# Revit family: BE_85013_de_DE
name_source: partatom
category: Leuchten
units: mm (PartAtom-declared; Revit-internal decimal feet)

## family parameters
Basisbauteil = Fläche
Beim Laden mit Abzugskörper schneiden = Ja
Bemaßung runder Anschluss = Durchmesser verwenden
Gemeinsam genutzt = Nein
Lichtquelle = Ja
Raumberechnungspunkt = Ja
Teiletyp = Normal

## types (4) — shared parameters
AC/DC = AC/DC
Aktualisierung = 2022-08-26T04:00:07
Anschlussleitung = 6.0 m H05RN-F 2 × 1²
Beschreibung = Aufsatzleuchte
Beschreibung_Sonderanfertigung = Hier können Sie Informationen zur Sonderanfertigung eintragen.
CE_Konformität = ja
Einstecktiefe = 65 mm
Energieeffizienzklasse = LED A++ - A
Farbfilter = 16777215
Farbtemperaturverschiebung bei Dämpfen der Lampe = <Keine Auswahl>
Farbwiedergabeindex = CRI > 80
Frequenz = 0/50-60 Hz
Gewicht = 8.15 kg
Hersteller = BEGA
Lampe = LED 24 W
Lastklassifizierung = Beleuchtung
Lebensdauerkriterien = L70B50 @ 25 °C = 175000 h
Logo = BEGA_Logo.png
Material_02 = BEGA_Oberfläche_Silber_matt
Material_03 = BEGA_Oberfläche_Weiss_matt
Material_06 = BEGA_Oberfläche_Edelstahl_gebürstet
Material_11 = BEGA_Glas_opal
Material_18 = BEGA_Gummi_schwarz
Neigungswinkel = 0.00°
Produktdatenblatt = https://cdn.bega.com
Scheinlast = 0 VA
Schutzart = IP 65
Schutzklasse = II
Sonderanfertigung = Nein
Spannung = 240 V
URL = https://www.bega.com
Umgebungstemperatur = 25 °C
zero-valued in all types: Vorgabe-Ansicht

## per-type parameters (varying)
| type | Bestellnummer | Datei für fotometrisches Netz | Farbtemperatur | LED_Modulbezeichnung | Lampenlichtstrom | Leuchtenlichtstrom | M_A | M_G | Modell |
| BEGA_85013_Grafit_K4 | 85013K4 | BE_85013K4.IES | 4000 K | LED-1281/840 | 4170 lm | 3433 lm | Nein | Ja | 85013K4 |
| BEGA_85013_Silber_K4 | 85013AK4 | BE_85013K4.IES | 4000 K | LED-1281/840 | 4170 lm | 3433 lm | Ja | Nein | 85013AK4 |
| BEGA_85013_Silber_K3 | 85013AK3 | BE_85013K3.IES | 3000 K | LED-1281/830 | 3970 lm | 3269 lm | Ja | Nein | 85013AK3 |
| BEGA_85013_Grafit_K3 | 85013K3 | BE_85013K3.IES | 3000 K | LED-1281/830 | 3970 lm | 3269 lm | Nein | Ja | 85013K3 |
